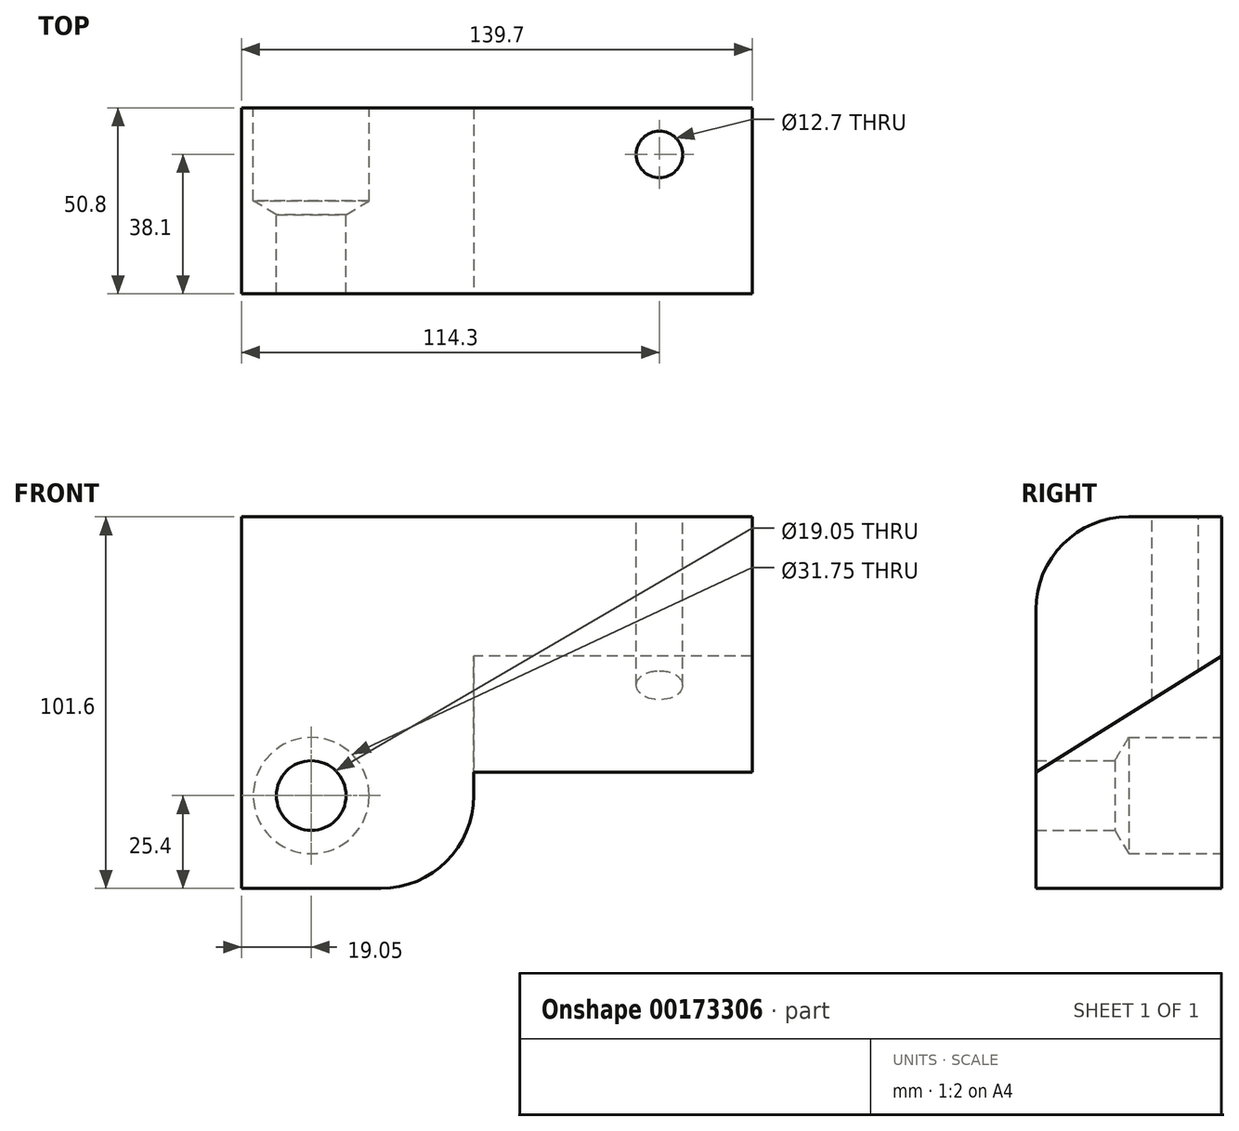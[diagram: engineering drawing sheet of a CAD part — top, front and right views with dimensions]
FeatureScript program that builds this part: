
annotation { "Feature Type Name" : "Feature", "Feature Type Description" : "" }
export const myFeature = defineFeature(function(context is Context, id is Id, definition is map)
    precondition{}
    {
        {
            var Q0;
            Q0=qCreatedBy(makeId("Right.planeOp"),FACE);
            var sketch = newSketch(context, id + "F0", { "sketchPlane" : qUnion([Q0])});
            skLineSegment(sketch, "E0", {"start": v(0, 0) * mm, "end": v(50.8, 0) * mm});
            skLineSegment(sketch, "E1", {"start": v(0, 0) * mm, "end": v(0, 31.75) * mm});
            skLineSegment(sketch, "E2", {"start": v(0, 31.75) * mm, "end": v(0, 63.5) * mm});
            skLineSegment(sketch, "E3", {"start": v(50.8, 0) * mm, "end": v(50.8, 101.6) * mm});
            skLineSegment(sketch, "E4", {"start": v(50.8, 63.5) * mm, "end": v(0, 31.75) * mm});
            skLineSegment(sketch, "E5", {"start": v(0, 24.88) * mm, "end": v(50.8, 24.88) * mm});
            skLineSegment(sketch, "E6", {"start": v(50.8, 101.6) * mm, "end": v(25.4, 101.6) * mm});
            skLineSegment(sketch, "E7", {"start": v(0, 76.2) * mm, "end": v(0, 63.5) * mm});
            skPoint(sketch, "E8.visualSharp", {"position": v(0, 101.6) * mm});
            skArc(sketch, "E8.filletArc", {"start": v(25.4, 101.6) * mm, "mid": v(7.44, 94.16) * mm, "end": v(0, 76.2) * mm});
            skSolve(sketch);
        }
        {
            var Q0;
            Q0=makeQuery(id+"F0.imprint","IMPRINT",FACE,{"disambiguationData":[TD([[makeQuery(id+"F0.imprint","IMPRINT",EDGE,{"derivedFrom":sQuery(id+"F0.wireOp",EDGE,"E2")}),-1.0]])]});
            extrude(context, id + "F1", {"entities" : qUnion([Q0]), "depth" : 139.7 * mm});
        }
        {
            var Q0;
            {var subQ0=sQuery(id+"F0.wireOp",EDGE,"E4");Q0=makeQuery(id+"F0.imprint","IMPRINT",FACE,{"disambiguationData":[TD([[makeQuery(id+"F0.imprint","IMPRINT",EDGE,{"derivedFrom":subQ0}),1.0]])]});}
            var Q1;
            {var subQ0=sQuery(id+"F0.wireOp",EDGE,"E0");Q1=makeQuery(id+"F0.imprint","IMPRINT",FACE,{"disambiguationData":[TD([[makeQuery(id+"F0.imprint","IMPRINT",EDGE,{"derivedFrom":subQ0}),1.0]])]});}
            extrude(context, id + "F2", {"entities" : qUnion([Q0, Q1]), "operationType" : NewBodyOperationType.ADD, "depth" : 63.5 * mm});
        }
        {
            var Q0;
            Q0=makeQuery(id+"F2.opExtrude","CAP_EDGE",EDGE,{"disambiguationData":[OSD([sQuery(id+"F0.wireOp",EDGE,"E0")])],"isStart":false});
            fillet(context, id + "F3", {"entities" : qUnion([Q0]), "radius" : 25.4 * mm, "tangentPropagation" : true, "allowEdgeOverflow" : false});
        }
        {
            var Q0;
            {var subQ0=sQuery(id+"F0.wireOp",EDGE,"E3");Q0=makeQuery(id+"F2.boolean.opBoolean","MERGE",FACE,{"derivedFrom":[makeQuery(id+"F1.opExtrude","SWEPT_FACE",FACE,{"disambiguationData":[OSD([subQ0])]}),makeQuery(id+"F2.opExtrude","SWEPT_FACE",FACE,{"disambiguationData":[OSD([subQ0])]})]});}
            var sketch = newSketch(context, id + "F4", { "sketchPlane" : qUnion([Q0])});
            skLineSegment(sketch, "E9", {"start": v(0, 0) * mm, "end": v(-19.05, 0) * mm});
            skLineSegment(sketch, "E10", {"start": v(0, 0) * mm, "end": v(0, 25.4) * mm});
            skLineSegment(sketch, "E11", {"start": v(0, 25.4) * mm, "end": v(-19.05, 25.4) * mm});
            skLineSegment(sketch, "E12", {"start": v(-19.05, 25.4) * mm, "end": v(-19.05, 0) * mm});
            skSolve(sketch);
        }
        {
            var Q0;
            Q0=sQuery(id+"F4.wireOp",VERTEX,"E12.start");
            var Q1;
            Q1=makeQuery(id+"F1.opExtrude","SWEPT_BODY",BODY,{"disambiguationData":[OSD([sQuery(id+"F0.wireOp",EDGE,"E2"),sQuery(id+"F0.wireOp",EDGE,"E3"),sQuery(id+"F0.wireOp",EDGE,"E4"),sQuery(id+"F0.wireOp",EDGE,"E6"),sQuery(id+"F0.wireOp",EDGE,"E7"),sQuery(id+"F0.wireOp",EDGE,"E8.filletArc")])]});
            hole(context, id + "F5", {"style" : HoleStyle.SIMPLE, "endStyle" : HoleEndStyle.THROUGH, "holeDiameter" : 19.05 * mm, "locations" : qUnion([Q0]), "scope" : qUnion([Q1]), "isTappedThrough" : true});
        }
        {
            var Q0;
            Q0=sQuery(id+"F4.wireOp",VERTEX,"E12.start");
            var Q1;
            Q1=makeQuery(id+"F1.opExtrude","SWEPT_BODY",BODY,{"disambiguationData":[OSD([sQuery(id+"F0.wireOp",EDGE,"E2"),sQuery(id+"F0.wireOp",EDGE,"E3"),sQuery(id+"F0.wireOp",EDGE,"E4"),sQuery(id+"F0.wireOp",EDGE,"E6"),sQuery(id+"F0.wireOp",EDGE,"E7"),sQuery(id+"F0.wireOp",EDGE,"E8.filletArc")])]});
            hole(context, id + "F6", {"style" : HoleStyle.SIMPLE, "endStyle" : HoleEndStyle.BLIND, "holeDiameter" : 31.75 * mm, "holeDepth" : 25.4 * mm, "locations" : qUnion([Q0]), "scope" : qUnion([Q1])});
        }
        {
            var Q0;
            Q0=makeQuery(id+"F1.opExtrude","SWEPT_FACE",FACE,{"disambiguationData":[OSD([sQuery(id+"F0.wireOp",EDGE,"E6")])]});
            var sketch = newSketch(context, id + "F7", { "sketchPlane" : qUnion([Q0])});
            skLineSegment(sketch, "E13", {"start": v(139.7, 50.8) * mm, "end": v(139.7, 38.1) * mm});
            skLineSegment(sketch, "E14", {"start": v(139.7, 50.8) * mm, "end": v(114.3, 50.8) * mm});
            skLineSegment(sketch, "E15", {"start": v(139.7, 38.1) * mm, "end": v(114.3, 38.1) * mm});
            skLineSegment(sketch, "E16", {"start": v(114.3, 38.1) * mm, "end": v(114.3, 50.8) * mm});
            skSolve(sketch);
        }
        {
            var Q0;
            Q0=sQuery(id+"F7.wireOp",VERTEX,"E16.start");
            var Q1;
            Q1=makeQuery(id+"F1.opExtrude","SWEPT_BODY",BODY,{"disambiguationData":[OSD([sQuery(id+"F0.wireOp",EDGE,"E2"),sQuery(id+"F0.wireOp",EDGE,"E3"),sQuery(id+"F0.wireOp",EDGE,"E4"),sQuery(id+"F0.wireOp",EDGE,"E6"),sQuery(id+"F0.wireOp",EDGE,"E7"),sQuery(id+"F0.wireOp",EDGE,"E8.filletArc")])]});
            hole(context, id + "F8", {"style" : HoleStyle.SIMPLE, "endStyle" : HoleEndStyle.THROUGH, "holeDiameter" : 12.7 * mm, "locations" : qUnion([Q0]), "scope" : qUnion([Q1]), "isTappedThrough" : true});
        }
    });
